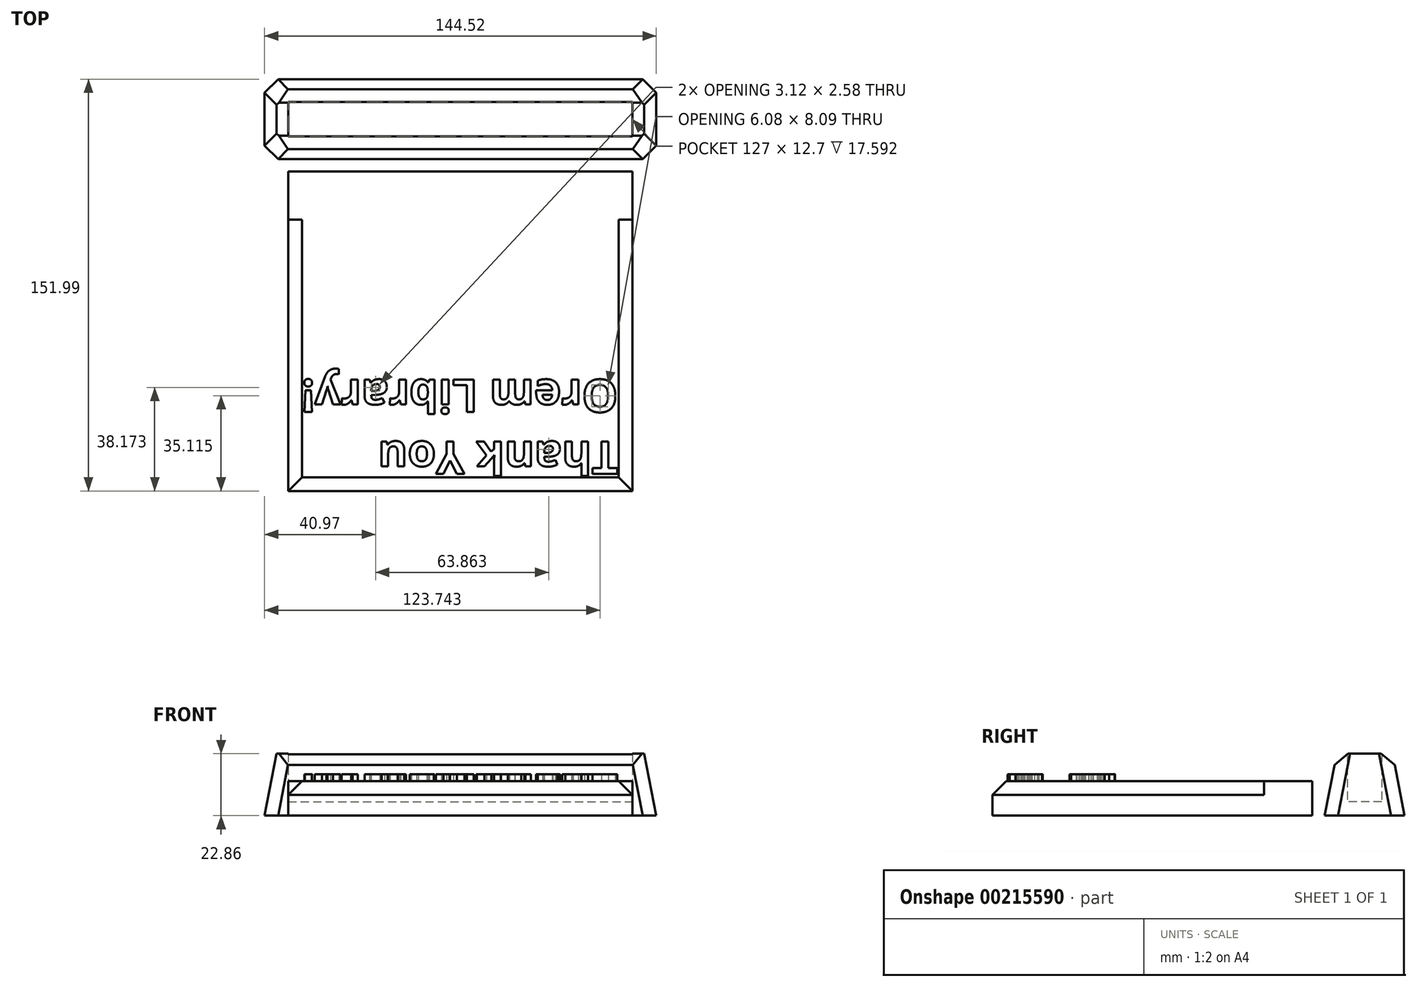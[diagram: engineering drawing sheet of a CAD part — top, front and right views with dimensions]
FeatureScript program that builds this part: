
annotation { "Feature Type Name" : "Feature", "Feature Type Description" : "" }
export const myFeature = defineFeature(function(context is Context, id is Id, definition is map)
    precondition{}
    {
        {
            var Q0;
            Q0=qCreatedBy(makeId("Top.planeOp"),FACE);
            var sketch = newSketch(context, id + "F0", { "sketchPlane" : qUnion([Q0])});
            skLineSegment(sketch, "E0.bottom", {"start": v(-63.5, 6.35) * mm, "end": v(63.5, 6.35) * mm});
            skLineSegment(sketch, "E0.top", {"start": v(-63.5, -6.35) * mm, "end": v(63.5, -6.35) * mm});
            skLineSegment(sketch, "E0.left", {"start": v(-63.5, 6.35) * mm, "end": v(-63.5, -6.35) * mm});
            skLineSegment(sketch, "E0.right", {"start": v(63.5, 6.35) * mm, "end": v(63.5, -6.35) * mm});
            skPoint(sketch, "E0.middle", {"position": v(0, 0) * mm});
            skSolve(sketch);
        }
        {
            var Q0;
            Q0=qCreatedBy(makeId("Top.planeOp"),FACE);
            var sketch = newSketch(context, id + "F1", { "sketchPlane" : qUnion([Q0])});
            skLineSegment(sketch, "E1.bottom", {"start": v(-67.81, 10.3) * mm, "end": v(67.81, 10.3) * mm});
            skLineSegment(sketch, "E1.top", {"start": v(-67.81, -10.3) * mm, "end": v(67.81, -10.3) * mm});
            skLineSegment(sketch, "E1.left", {"start": v(-67.81, 10.3) * mm, "end": v(-67.81, -10.3) * mm});
            skLineSegment(sketch, "E1.right", {"start": v(67.81, 10.3) * mm, "end": v(67.81, -10.3) * mm});
            skPoint(sketch, "E1.middle", {"position": v(0, 0) * mm});
            skSolve(sketch);
        }
        {
            var Q0;
            Q0=makeQuery(id+"F1.imprint","IMPRINT",FACE,{"disambiguationData":[TD([[makeQuery(id+"F1.imprint","IMPRINT",EDGE,{"derivedFrom":sQuery(id+"F1.wireOp",EDGE,"E1.bottom")}),-1.0]])]});
            extrude(context, id + "F2", {"entities" : qUnion([Q0]), "depth" : 22.86 * mm});
        }
        {
            var Q0;
            Q0=makeQuery(id+"F2.opExtrude","CAP_FACE",FACE,{"disambiguationData":[OSD([sQuery(id+"F1.wireOp",EDGE,"E1.bottom"),sQuery(id+"F1.wireOp",EDGE,"E1.top"),sQuery(id+"F1.wireOp",EDGE,"E1.left"),sQuery(id+"F1.wireOp",EDGE,"E1.right")])],"isStart":false});
            extrude(context, id + "F3", {"entities" : qUnion([Q0]), "operationType" : NewBodyOperationType.ADD, "oppositeDirection" : true, "depth" : 22.86 * mm, "hasDraft" : true, "draftAngle" : 11 * degree});
        }
        {
            var Q0;
            Q0=makeQuery(id+"F0.imprint","IMPRINT",FACE,{"disambiguationData":[TD([[makeQuery(id+"F0.imprint","IMPRINT",EDGE,{"derivedFrom":sQuery(id+"F0.wireOp",EDGE,"E0.bottom")}),-1.0]])]});
            extrude(context, id + "F4", {"entities" : qUnion([Q0]), "operationType" : NewBodyOperationType.REMOVE, "depth" : 25.4 * mm, "hasSecondDirection" : true, "secondDirectionOppositeDirection" : false, "secondDirectionDepth" : 5.08 * mm});
        }
        {
            var Q0;
            Q0=makeQuery(id+"F3.opExtrude","SWEPT_EDGE",EDGE,{"disambiguationData":[OSD([sQuery(id+"F1.wireOp",EDGE,"E1.top"),sQuery(id+"F1.wireOp",EDGE,"E1.left")])]});
            var Q1;
            Q1=makeQuery(id+"F3.opExtrude","SWEPT_EDGE",EDGE,{"disambiguationData":[OSD([sQuery(id+"F1.wireOp",EDGE,"E1.bottom"),sQuery(id+"F1.wireOp",EDGE,"E1.left")])]});
            var Q2;
            Q2=makeQuery(id+"F3.opExtrude","SWEPT_EDGE",EDGE,{"disambiguationData":[OSD([sQuery(id+"F1.wireOp",EDGE,"E1.top"),sQuery(id+"F1.wireOp",EDGE,"E1.right")])]});
            var Q3;
            Q3=makeQuery(id+"F3.opExtrude","SWEPT_EDGE",EDGE,{"disambiguationData":[OSD([sQuery(id+"F1.wireOp",EDGE,"E1.bottom"),sQuery(id+"F1.wireOp",EDGE,"E1.right")])]});
            var Q4;
            {var subQ0=sQuery(id+"F1.wireOp",EDGE,"E1.top");Q4=makeQuery(id+"F3.boolean.opBoolean","MERGE",EDGE,{"derivedFrom":[makeQuery(id+"F2.opExtrude","CAP_EDGE",EDGE,{"disambiguationData":[OSD([subQ0])],"isStart":false}),makeQuery(id+"F3.opExtrude","CAP_EDGE",EDGE,{"disambiguationData":[OSD([subQ0])],"isStart":true})]});}
            var Q5;
            {var subQ0=sQuery(id+"F1.wireOp",EDGE,"E1.bottom");Q5=makeQuery(id+"F3.boolean.opBoolean","MERGE",EDGE,{"derivedFrom":[makeQuery(id+"F2.opExtrude","CAP_EDGE",EDGE,{"disambiguationData":[OSD([subQ0])],"isStart":false}),makeQuery(id+"F3.opExtrude","CAP_EDGE",EDGE,{"disambiguationData":[OSD([subQ0])],"isStart":true})]});}
            chamfer(context, id + "F5", {"entities" : qUnion([Q0, Q1, Q2, Q3, Q4, Q5]), "width" : 5.08 * mm, "tangentPropagation" : true});
        }
        {
            var Q0;
            Q0=makeQuery(id+"F2.opExtrude","SWEPT_BODY",BODY,{"disambiguationData":[OSD([sQuery(id+"F1.wireOp",EDGE,"E1.bottom"),sQuery(id+"F1.wireOp",EDGE,"E1.top"),sQuery(id+"F1.wireOp",EDGE,"E1.left"),sQuery(id+"F1.wireOp",EDGE,"E1.right")])]});
            transform(context, id + "F6", {"entities" : qUnion([Q0]), "transformType" : TransformType.TRANSLATION_3D, "dx" : 0 * mm, "dy" : 56.13 * mm, "dz" : 0 * mm, "makeCopy" : false});
        }
        {
            var Q0;
            Q0=qCreatedBy(makeId("Top.planeOp"),FACE);
            var sketch = newSketch(context, id + "F7", { "sketchPlane" : qUnion([Q0])});
            skLineSegment(sketch, "E2.bottom", {"start": v(-63.5, 36.8) * mm, "end": v(63.5, 36.8) * mm});
            skLineSegment(sketch, "E2.top", {"start": v(-63.5, -81.1) * mm, "end": v(63.5, -81.1) * mm});
            skLineSegment(sketch, "E2.left", {"start": v(-63.5, 36.8) * mm, "end": v(-63.5, -81.1) * mm});
            skLineSegment(sketch, "E2.right", {"start": v(63.5, 36.8) * mm, "end": v(63.5, -81.1) * mm});
            skPoint(sketch, "E2.middle", {"position": v(0, -22.14) * mm});
            skSolve(sketch);
        }
        {
            var Q0;
            Q0=makeQuery(id+"F7.imprint","IMPRINT",FACE,{"disambiguationData":[TD([[makeQuery(id+"F7.imprint","IMPRINT",EDGE,{"derivedFrom":sQuery(id+"F7.wireOp",EDGE,"E2.bottom")}),-1.0]])]});
            extrude(context, id + "F8", {"entities" : qUnion([Q0]), "depth" : 12.7 * mm});
        }
        {
            var Q0;
            Q0=makeQuery(id+"F8.opExtrude","CAP_EDGE",EDGE,{"disambiguationData":[OSD([sQuery(id+"F7.wireOp",EDGE,"E2.top")])],"isStart":false});
            var Q1;
            Q1=makeQuery(id+"F8.opExtrude","CAP_EDGE",EDGE,{"disambiguationData":[OSD([sQuery(id+"F7.wireOp",EDGE,"E2.right")])],"isStart":false});
            var Q2;
            Q2=makeQuery(id+"F8.opExtrude","CAP_EDGE",EDGE,{"disambiguationData":[OSD([sQuery(id+"F7.wireOp",EDGE,"E2.left")])],"isStart":false});
            chamfer(context, id + "F9", {"entities" : qUnion([Q0, Q1, Q2]), "width" : 5.08 * mm, "tangentPropagation" : true});
        }
        {
            var Q0;
            Q0=makeQuery(id+"F8.opExtrude","SWEPT_FACE",FACE,{"disambiguationData":[OSD([sQuery(id+"F7.wireOp",EDGE,"E2.bottom")])]});
            var sketch = newSketch(context, id + "F10", { "sketchPlane" : qUnion([Q0])});
            skLineSegment(sketch, "E3.bottom", {"start": v(-63.5, 0) * mm, "end": v(-10.71, 0) * mm});
            skLineSegment(sketch, "E3.top", {"start": v(-63.5, 12.7) * mm, "end": v(-10.71, 12.7) * mm});
            skLineSegment(sketch, "E3.left", {"start": v(-63.5, 0) * mm, "end": v(-63.5, 12.7) * mm});
            skLineSegment(sketch, "E3.right", {"start": v(-10.71, 0) * mm, "end": v(-10.71, 12.7) * mm});
            skLineSegment(sketch, "E4.bottom", {"start": v(-10.71, 12.7) * mm, "end": v(63.5, 12.7) * mm});
            skLineSegment(sketch, "E4.top", {"start": v(-10.71, 0) * mm, "end": v(63.5, 0) * mm});
            skLineSegment(sketch, "E4.left", {"start": v(-10.71, 12.7) * mm, "end": v(-10.71, 0) * mm});
            skLineSegment(sketch, "E4.right", {"start": v(63.5, 12.7) * mm, "end": v(63.5, 0) * mm});
            skSolve(sketch);
        }
        {
            var Q0;
            {var subQ1=makeQuery(id+"F9.opChamfer","BLEND_EDGE",EDGE,{"blendedFrom":[makeQuery(id+"F8.opExtrude","CAP_EDGE",EDGE,{"disambiguationData":[OSD([sQuery(id+"F7.wireOp",EDGE,"E2.right")])],"isStart":false}),makeQuery(id+"F8.opExtrude","SWEPT_FACE",FACE,{"disambiguationData":[OSD([sQuery(id+"F7.wireOp",EDGE,"E2.bottom")])]})],"blendedInto":[makeQuery(id+"F8.opExtrude","SWEPT_FACE",FACE,{"disambiguationData":[OSD([sQuery(id+"F7.wireOp",EDGE,"E2.bottom")])]})]});Q0=makeQuery(id+"F10.imprint","IMPRINT",FACE,{"disambiguationData":[TD([[makeQuery(id+"F10.imprint","IMPRINT",EDGE,{"derivedFrom":subQ1}),-1.0]])]});}
            var Q1;
            {var subQ2=sQuery(id+"F10.wireOp",EDGE,"E3.bottom");Q1=makeQuery(id+"F10.imprint","IMPRINT",FACE,{"disambiguationData":[TD([[makeQuery(id+"F10.imprint","IMPRINT",EDGE,{"derivedFrom":subQ2}),-1.0]])]});}
            var Q2;
            {var subQ1=makeQuery(id+"F9.opChamfer","BLEND_EDGE",EDGE,{"blendedFrom":[makeQuery(id+"F8.opExtrude","CAP_EDGE",EDGE,{"disambiguationData":[OSD([sQuery(id+"F7.wireOp",EDGE,"E2.left")])],"isStart":false}),makeQuery(id+"F8.opExtrude","SWEPT_FACE",FACE,{"disambiguationData":[OSD([sQuery(id+"F7.wireOp",EDGE,"E2.bottom")])]})],"blendedInto":[makeQuery(id+"F8.opExtrude","SWEPT_FACE",FACE,{"disambiguationData":[OSD([sQuery(id+"F7.wireOp",EDGE,"E2.bottom")])]})]});Q2=makeQuery(id+"F10.imprint","IMPRINT",FACE,{"disambiguationData":[TD([[makeQuery(id+"F10.imprint","IMPRINT",EDGE,{"derivedFrom":subQ1}),-1.0]])]});}
            var Q3;
            {var subQ1=sQuery(id+"F10.wireOp",EDGE,"E4.top");Q3=makeQuery(id+"F10.imprint","IMPRINT",FACE,{"disambiguationData":[TD([[makeQuery(id+"F10.imprint","IMPRINT",EDGE,{"derivedFrom":subQ1}),-1.0]])]});}
            extrude(context, id + "F11", {"entities" : qUnion([Q0, Q1, Q2, Q3]), "operationType" : NewBodyOperationType.ADD, "oppositeDirection" : true, "depth" : 17.78 * mm});
        }
        {
            var Q0;
            Q0=makeQuery(id+"F11.boolean.opBoolean","MERGE",FACE,{"derivedFrom":[makeQuery(id+"F8.opExtrude","CAP_FACE",FACE,{"disambiguationData":[OSD([sQuery(id+"F7.wireOp",EDGE,"E2.bottom"),sQuery(id+"F7.wireOp",EDGE,"E2.top"),sQuery(id+"F7.wireOp",EDGE,"E2.left"),sQuery(id+"F7.wireOp",EDGE,"E2.right")])],"isStart":false}),makeQuery(id+"F11.opExtrude","SWEPT_FACE",FACE,{"disambiguationData":[OSD([sQuery(id+"F10.wireOp",EDGE,"E3.top"),sQuery(id+"F10.wireOp",EDGE,"E4.bottom")])]})]});
            var sketch = newSketch(context, id + "F12", { "sketchPlane" : qUnion([Q0])});
            skText(sketch, "E5", { "text": "Thank You\nOrem Library!", "fontName": "OpenSans-Bold.ttf"});
            const initialGuessF12  = {"E5": [-0.05842, -0.07602, 1, 0, 0.01209]};
            skSetInitialGuess(sketch, initialGuessF12);
            skSolve(sketch);
        }
        {
            var Q0;
            Q0 = qSketchRegion(id + "F12", true);
            extrude(context, id + "F13", {"entities" : qUnion([Q0]), "depth" : 2.54 * mm});
        }
        {
            var Q0;
            Q0=makeQuery(id+"F13.opExtrude","SWEPT_BODY",BODY,{"disambiguationData":[OSD([sQuery(id+"F12.wireOp",EDGE,"E5.sketch_text.stroke-0"),sQuery(id+"F12.wireOp",EDGE,"E5.sketch_text.stroke-1"),sQuery(id+"F12.wireOp",EDGE,"E5.sketch_text.stroke-2"),sQuery(id+"F12.wireOp",EDGE,"E5.sketch_text.stroke-3"),sQuery(id+"F12.wireOp",EDGE,"E5.sketch_text.stroke-4"),sQuery(id+"F12.wireOp",EDGE,"E5.sketch_text.stroke-5"),sQuery(id+"F12.wireOp",EDGE,"E5.sketch_text.stroke-6"),sQuery(id+"F12.wireOp",EDGE,"E5.sketch_text.stroke-7")])]});
            var Q1;
            Q1=makeQuery(id+"F13.opExtrude","SWEPT_BODY",BODY,{"disambiguationData":[OSD([sQuery(id+"F12.wireOp",EDGE,"E5.sketch_text.stroke-8"),sQuery(id+"F12.wireOp",EDGE,"E5.sketch_text.stroke-9"),sQuery(id+"F12.wireOp",EDGE,"E5.sketch_text.stroke-10"),sQuery(id+"F12.wireOp",EDGE,"E5.sketch_text.stroke-11"),sQuery(id+"F12.wireOp",EDGE,"E5.sketch_text.stroke-12"),sQuery(id+"F12.wireOp",EDGE,"E5.sketch_text.stroke-13"),sQuery(id+"F12.wireOp",EDGE,"E5.sketch_text.stroke-14"),sQuery(id+"F12.wireOp",EDGE,"E5.sketch_text.stroke-15"),sQuery(id+"F12.wireOp",EDGE,"E5.sketch_text.stroke-16"),sQuery(id+"F12.wireOp",EDGE,"E5.sketch_text.stroke-17"),sQuery(id+"F12.wireOp",EDGE,"E5.sketch_text.stroke-18"),sQuery(id+"F12.wireOp",EDGE,"E5.sketch_text.stroke-19"),sQuery(id+"F12.wireOp",EDGE,"E5.sketch_text.stroke-20"),sQuery(id+"F12.wireOp",EDGE,"E5.sketch_text.stroke-21"),sQuery(id+"F12.wireOp",EDGE,"E5.sketch_text.stroke-22"),sQuery(id+"F12.wireOp",EDGE,"E5.sketch_text.stroke-23"),sQuery(id+"F12.wireOp",EDGE,"E5.sketch_text.stroke-24")])]});
            var Q2;
            Q2=makeQuery(id+"F13.opExtrude","SWEPT_BODY",BODY,{"disambiguationData":[OSD([sQuery(id+"F12.wireOp",EDGE,"E5.sketch_text.stroke-25"),sQuery(id+"F12.wireOp",EDGE,"E5.sketch_text.stroke-26"),sQuery(id+"F12.wireOp",EDGE,"E5.sketch_text.stroke-27"),sQuery(id+"F12.wireOp",EDGE,"E5.sketch_text.stroke-28"),sQuery(id+"F12.wireOp",EDGE,"E5.sketch_text.stroke-29"),sQuery(id+"F12.wireOp",EDGE,"E5.sketch_text.stroke-30"),sQuery(id+"F12.wireOp",EDGE,"E5.sketch_text.stroke-31"),sQuery(id+"F12.wireOp",EDGE,"E5.sketch_text.stroke-32"),sQuery(id+"F12.wireOp",EDGE,"E5.sketch_text.stroke-33"),sQuery(id+"F12.wireOp",EDGE,"E5.sketch_text.stroke-34"),sQuery(id+"F12.wireOp",EDGE,"E5.sketch_text.stroke-35"),sQuery(id+"F12.wireOp",EDGE,"E5.sketch_text.stroke-36"),sQuery(id+"F12.wireOp",EDGE,"E5.sketch_text.stroke-37"),sQuery(id+"F12.wireOp",EDGE,"E5.sketch_text.stroke-38"),sQuery(id+"F12.wireOp",EDGE,"E5.sketch_text.stroke-39"),sQuery(id+"F12.wireOp",EDGE,"E5.sketch_text.stroke-40"),sQuery(id+"F12.wireOp",EDGE,"E5.sketch_text.stroke-41"),sQuery(id+"F12.wireOp",EDGE,"E5.sketch_text.stroke-42"),sQuery(id+"F12.wireOp",EDGE,"E5.sketch_text.stroke-43"),sQuery(id+"F12.wireOp",EDGE,"E5.sketch_text.stroke-44"),sQuery(id+"F12.wireOp",EDGE,"E5.sketch_text.stroke-45"),sQuery(id+"F12.wireOp",EDGE,"E5.sketch_text.stroke-46"),sQuery(id+"F12.wireOp",EDGE,"E5.sketch_text.stroke-47"),sQuery(id+"F12.wireOp",EDGE,"E5.sketch_text.stroke-48"),sQuery(id+"F12.wireOp",EDGE,"E5.sketch_text.stroke-49")])]});
            var Q3;
            Q3=makeQuery(id+"F13.opExtrude","SWEPT_BODY",BODY,{"disambiguationData":[OSD([sQuery(id+"F12.wireOp",EDGE,"E5.sketch_text.stroke-50"),sQuery(id+"F12.wireOp",EDGE,"E5.sketch_text.stroke-51"),sQuery(id+"F12.wireOp",EDGE,"E5.sketch_text.stroke-52"),sQuery(id+"F12.wireOp",EDGE,"E5.sketch_text.stroke-53"),sQuery(id+"F12.wireOp",EDGE,"E5.sketch_text.stroke-54"),sQuery(id+"F12.wireOp",EDGE,"E5.sketch_text.stroke-55"),sQuery(id+"F12.wireOp",EDGE,"E5.sketch_text.stroke-56"),sQuery(id+"F12.wireOp",EDGE,"E5.sketch_text.stroke-57"),sQuery(id+"F12.wireOp",EDGE,"E5.sketch_text.stroke-58"),sQuery(id+"F12.wireOp",EDGE,"E5.sketch_text.stroke-59"),sQuery(id+"F12.wireOp",EDGE,"E5.sketch_text.stroke-60"),sQuery(id+"F12.wireOp",EDGE,"E5.sketch_text.stroke-61"),sQuery(id+"F12.wireOp",EDGE,"E5.sketch_text.stroke-62"),sQuery(id+"F12.wireOp",EDGE,"E5.sketch_text.stroke-63"),sQuery(id+"F12.wireOp",EDGE,"E5.sketch_text.stroke-64"),sQuery(id+"F12.wireOp",EDGE,"E5.sketch_text.stroke-65"),sQuery(id+"F12.wireOp",EDGE,"E5.sketch_text.stroke-66")])]});
            var Q4;
            Q4=makeQuery(id+"F13.opExtrude","SWEPT_BODY",BODY,{"disambiguationData":[OSD([sQuery(id+"F12.wireOp",EDGE,"E5.sketch_text.stroke-67"),sQuery(id+"F12.wireOp",EDGE,"E5.sketch_text.stroke-68"),sQuery(id+"F12.wireOp",EDGE,"E5.sketch_text.stroke-69"),sQuery(id+"F12.wireOp",EDGE,"E5.sketch_text.stroke-70"),sQuery(id+"F12.wireOp",EDGE,"E5.sketch_text.stroke-71"),sQuery(id+"F12.wireOp",EDGE,"E5.sketch_text.stroke-72"),sQuery(id+"F12.wireOp",EDGE,"E5.sketch_text.stroke-73"),sQuery(id+"F12.wireOp",EDGE,"E5.sketch_text.stroke-74"),sQuery(id+"F12.wireOp",EDGE,"E5.sketch_text.stroke-75"),sQuery(id+"F12.wireOp",EDGE,"E5.sketch_text.stroke-76"),sQuery(id+"F12.wireOp",EDGE,"E5.sketch_text.stroke-77"),sQuery(id+"F12.wireOp",EDGE,"E5.sketch_text.stroke-78"),sQuery(id+"F12.wireOp",EDGE,"E5.sketch_text.stroke-79"),sQuery(id+"F12.wireOp",EDGE,"E5.sketch_text.stroke-80"),sQuery(id+"F12.wireOp",EDGE,"E5.sketch_text.stroke-81")])]});
            var Q5;
            Q5=makeQuery(id+"F13.opExtrude","SWEPT_BODY",BODY,{"disambiguationData":[OSD([sQuery(id+"F12.wireOp",EDGE,"E5.sketch_text.stroke-82"),sQuery(id+"F12.wireOp",EDGE,"E5.sketch_text.stroke-83"),sQuery(id+"F12.wireOp",EDGE,"E5.sketch_text.stroke-84"),sQuery(id+"F12.wireOp",EDGE,"E5.sketch_text.stroke-85"),sQuery(id+"F12.wireOp",EDGE,"E5.sketch_text.stroke-86"),sQuery(id+"F12.wireOp",EDGE,"E5.sketch_text.stroke-87"),sQuery(id+"F12.wireOp",EDGE,"E5.sketch_text.stroke-88"),sQuery(id+"F12.wireOp",EDGE,"E5.sketch_text.stroke-89"),sQuery(id+"F12.wireOp",EDGE,"E5.sketch_text.stroke-90")])]});
            var Q6;
            Q6=makeQuery(id+"F13.opExtrude","SWEPT_BODY",BODY,{"disambiguationData":[OSD([sQuery(id+"F12.wireOp",EDGE,"E5.sketch_text.stroke-91"),sQuery(id+"F12.wireOp",EDGE,"E5.sketch_text.stroke-92"),sQuery(id+"F12.wireOp",EDGE,"E5.sketch_text.stroke-93"),sQuery(id+"F12.wireOp",EDGE,"E5.sketch_text.stroke-94"),sQuery(id+"F12.wireOp",EDGE,"E5.sketch_text.stroke-95"),sQuery(id+"F12.wireOp",EDGE,"E5.sketch_text.stroke-96"),sQuery(id+"F12.wireOp",EDGE,"E5.sketch_text.stroke-97"),sQuery(id+"F12.wireOp",EDGE,"E5.sketch_text.stroke-98"),sQuery(id+"F12.wireOp",EDGE,"E5.sketch_text.stroke-99"),sQuery(id+"F12.wireOp",EDGE,"E5.sketch_text.stroke-100"),sQuery(id+"F12.wireOp",EDGE,"E5.sketch_text.stroke-101"),sQuery(id+"F12.wireOp",EDGE,"E5.sketch_text.stroke-102"),sQuery(id+"F12.wireOp",EDGE,"E5.sketch_text.stroke-103"),sQuery(id+"F12.wireOp",EDGE,"E5.sketch_text.stroke-104"),sQuery(id+"F12.wireOp",EDGE,"E5.sketch_text.stroke-105"),sQuery(id+"F12.wireOp",EDGE,"E5.sketch_text.stroke-106"),sQuery(id+"F12.wireOp",EDGE,"E5.sketch_text.stroke-107"),sQuery(id+"F12.wireOp",EDGE,"E5.sketch_text.stroke-108")])]});
            var Q7;
            Q7=makeQuery(id+"F13.opExtrude","SWEPT_BODY",BODY,{"disambiguationData":[OSD([sQuery(id+"F12.wireOp",EDGE,"E5.sketch_text.stroke-109"),sQuery(id+"F12.wireOp",EDGE,"E5.sketch_text.stroke-110"),sQuery(id+"F12.wireOp",EDGE,"E5.sketch_text.stroke-111"),sQuery(id+"F12.wireOp",EDGE,"E5.sketch_text.stroke-112"),sQuery(id+"F12.wireOp",EDGE,"E5.sketch_text.stroke-113"),sQuery(id+"F12.wireOp",EDGE,"E5.sketch_text.stroke-114"),sQuery(id+"F12.wireOp",EDGE,"E5.sketch_text.stroke-115"),sQuery(id+"F12.wireOp",EDGE,"E5.sketch_text.stroke-116"),sQuery(id+"F12.wireOp",EDGE,"E5.sketch_text.stroke-117"),sQuery(id+"F12.wireOp",EDGE,"E5.sketch_text.stroke-118"),sQuery(id+"F12.wireOp",EDGE,"E5.sketch_text.stroke-119"),sQuery(id+"F12.wireOp",EDGE,"E5.sketch_text.stroke-120"),sQuery(id+"F12.wireOp",EDGE,"E5.sketch_text.stroke-121"),sQuery(id+"F12.wireOp",EDGE,"E5.sketch_text.stroke-122"),sQuery(id+"F12.wireOp",EDGE,"E5.sketch_text.stroke-123"),sQuery(id+"F12.wireOp",EDGE,"E5.sketch_text.stroke-124"),sQuery(id+"F12.wireOp",EDGE,"E5.sketch_text.stroke-125")])]});
            var Q8;
            Q8=makeQuery(id+"F13.opExtrude","SWEPT_BODY",BODY,{"disambiguationData":[OSD([sQuery(id+"F12.wireOp",EDGE,"E5.sketch_text.stroke-126"),sQuery(id+"F12.wireOp",EDGE,"E5.sketch_text.stroke-127"),sQuery(id+"F12.wireOp",EDGE,"E5.sketch_text.stroke-128"),sQuery(id+"F12.wireOp",EDGE,"E5.sketch_text.stroke-129"),sQuery(id+"F12.wireOp",EDGE,"E5.sketch_text.stroke-130"),sQuery(id+"F12.wireOp",EDGE,"E5.sketch_text.stroke-131"),sQuery(id+"F12.wireOp",EDGE,"E5.sketch_text.stroke-132"),sQuery(id+"F12.wireOp",EDGE,"E5.sketch_text.stroke-133"),sQuery(id+"F12.wireOp",EDGE,"E5.sketch_text.stroke-134"),sQuery(id+"F12.wireOp",EDGE,"E5.sketch_text.stroke-135"),sQuery(id+"F12.wireOp",EDGE,"E5.sketch_text.stroke-136"),sQuery(id+"F12.wireOp",EDGE,"E5.sketch_text.stroke-137"),sQuery(id+"F12.wireOp",EDGE,"E5.sketch_text.stroke-138"),sQuery(id+"F12.wireOp",EDGE,"E5.sketch_text.stroke-139")])]});
            var Q9;
            Q9=makeQuery(id+"F13.opExtrude","SWEPT_BODY",BODY,{"disambiguationData":[OSD([sQuery(id+"F12.wireOp",EDGE,"E5.sketch_text.stroke-140"),sQuery(id+"F12.wireOp",EDGE,"E5.sketch_text.stroke-141"),sQuery(id+"F12.wireOp",EDGE,"E5.sketch_text.stroke-142"),sQuery(id+"F12.wireOp",EDGE,"E5.sketch_text.stroke-143"),sQuery(id+"F12.wireOp",EDGE,"E5.sketch_text.stroke-144"),sQuery(id+"F12.wireOp",EDGE,"E5.sketch_text.stroke-145"),sQuery(id+"F12.wireOp",EDGE,"E5.sketch_text.stroke-146"),sQuery(id+"F12.wireOp",EDGE,"E5.sketch_text.stroke-147"),sQuery(id+"F12.wireOp",EDGE,"E5.sketch_text.stroke-148"),sQuery(id+"F12.wireOp",EDGE,"E5.sketch_text.stroke-149"),sQuery(id+"F12.wireOp",EDGE,"E5.sketch_text.stroke-150"),sQuery(id+"F12.wireOp",EDGE,"E5.sketch_text.stroke-151"),sQuery(id+"F12.wireOp",EDGE,"E5.sketch_text.stroke-152")])]});
            var Q10;
            Q10=makeQuery(id+"F13.opExtrude","SWEPT_BODY",BODY,{"disambiguationData":[OSD([sQuery(id+"F12.wireOp",EDGE,"E5.sketch_text.stroke-153"),sQuery(id+"F12.wireOp",EDGE,"E5.sketch_text.stroke-154"),sQuery(id+"F12.wireOp",EDGE,"E5.sketch_text.stroke-155"),sQuery(id+"F12.wireOp",EDGE,"E5.sketch_text.stroke-156"),sQuery(id+"F12.wireOp",EDGE,"E5.sketch_text.stroke-157"),sQuery(id+"F12.wireOp",EDGE,"E5.sketch_text.stroke-158"),sQuery(id+"F12.wireOp",EDGE,"E5.sketch_text.stroke-159"),sQuery(id+"F12.wireOp",EDGE,"E5.sketch_text.stroke-160"),sQuery(id+"F12.wireOp",EDGE,"E5.sketch_text.stroke-161"),sQuery(id+"F12.wireOp",EDGE,"E5.sketch_text.stroke-162"),sQuery(id+"F12.wireOp",EDGE,"E5.sketch_text.stroke-163"),sQuery(id+"F12.wireOp",EDGE,"E5.sketch_text.stroke-164"),sQuery(id+"F12.wireOp",EDGE,"E5.sketch_text.stroke-165"),sQuery(id+"F12.wireOp",EDGE,"E5.sketch_text.stroke-166"),sQuery(id+"F12.wireOp",EDGE,"E5.sketch_text.stroke-167"),sQuery(id+"F12.wireOp",EDGE,"E5.sketch_text.stroke-168"),sQuery(id+"F12.wireOp",EDGE,"E5.sketch_text.stroke-169"),sQuery(id+"F12.wireOp",EDGE,"E5.sketch_text.stroke-170"),sQuery(id+"F12.wireOp",EDGE,"E5.sketch_text.stroke-171"),sQuery(id+"F12.wireOp",EDGE,"E5.sketch_text.stroke-172")])]});
            var Q11;
            Q11=makeQuery(id+"F13.opExtrude","SWEPT_BODY",BODY,{"disambiguationData":[OSD([sQuery(id+"F12.wireOp",EDGE,"E5.sketch_text.stroke-173"),sQuery(id+"F12.wireOp",EDGE,"E5.sketch_text.stroke-174"),sQuery(id+"F12.wireOp",EDGE,"E5.sketch_text.stroke-175"),sQuery(id+"F12.wireOp",EDGE,"E5.sketch_text.stroke-176"),sQuery(id+"F12.wireOp",EDGE,"E5.sketch_text.stroke-177"),sQuery(id+"F12.wireOp",EDGE,"E5.sketch_text.stroke-178"),sQuery(id+"F12.wireOp",EDGE,"E5.sketch_text.stroke-179"),sQuery(id+"F12.wireOp",EDGE,"E5.sketch_text.stroke-180"),sQuery(id+"F12.wireOp",EDGE,"E5.sketch_text.stroke-181"),sQuery(id+"F12.wireOp",EDGE,"E5.sketch_text.stroke-182"),sQuery(id+"F12.wireOp",EDGE,"E5.sketch_text.stroke-183"),sQuery(id+"F12.wireOp",EDGE,"E5.sketch_text.stroke-184"),sQuery(id+"F12.wireOp",EDGE,"E5.sketch_text.stroke-185"),sQuery(id+"F12.wireOp",EDGE,"E5.sketch_text.stroke-186"),sQuery(id+"F12.wireOp",EDGE,"E5.sketch_text.stroke-187"),sQuery(id+"F12.wireOp",EDGE,"E5.sketch_text.stroke-188"),sQuery(id+"F12.wireOp",EDGE,"E5.sketch_text.stroke-189"),sQuery(id+"F12.wireOp",EDGE,"E5.sketch_text.stroke-190"),sQuery(id+"F12.wireOp",EDGE,"E5.sketch_text.stroke-191"),sQuery(id+"F12.wireOp",EDGE,"E5.sketch_text.stroke-192"),sQuery(id+"F12.wireOp",EDGE,"E5.sketch_text.stroke-193"),sQuery(id+"F12.wireOp",EDGE,"E5.sketch_text.stroke-194"),sQuery(id+"F12.wireOp",EDGE,"E5.sketch_text.stroke-195"),sQuery(id+"F12.wireOp",EDGE,"E5.sketch_text.stroke-196"),sQuery(id+"F12.wireOp",EDGE,"E5.sketch_text.stroke-197"),sQuery(id+"F12.wireOp",EDGE,"E5.sketch_text.stroke-198"),sQuery(id+"F12.wireOp",EDGE,"E5.sketch_text.stroke-199"),sQuery(id+"F12.wireOp",EDGE,"E5.sketch_text.stroke-200")])]});
            var Q12;
            Q12=makeQuery(id+"F13.opExtrude","SWEPT_BODY",BODY,{"disambiguationData":[OSD([sQuery(id+"F12.wireOp",EDGE,"E5.sketch_text.stroke-201"),sQuery(id+"F12.wireOp",EDGE,"E5.sketch_text.stroke-202"),sQuery(id+"F12.wireOp",EDGE,"E5.sketch_text.stroke-203"),sQuery(id+"F12.wireOp",EDGE,"E5.sketch_text.stroke-204"),sQuery(id+"F12.wireOp",EDGE,"E5.sketch_text.stroke-205"),sQuery(id+"F12.wireOp",EDGE,"E5.sketch_text.stroke-206")])]});
            var Q13;
            Q13=makeQuery(id+"F13.opExtrude","SWEPT_BODY",BODY,{"disambiguationData":[OSD([sQuery(id+"F12.wireOp",EDGE,"E5.sketch_text.stroke-207"),sQuery(id+"F12.wireOp",EDGE,"E5.sketch_text.stroke-208"),sQuery(id+"F12.wireOp",EDGE,"E5.sketch_text.stroke-209"),sQuery(id+"F12.wireOp",EDGE,"E5.sketch_text.stroke-210"),sQuery(id+"F12.wireOp",EDGE,"E5.sketch_text.stroke-211")])]});
            var Q14;
            Q14=makeQuery(id+"F13.opExtrude","SWEPT_BODY",BODY,{"disambiguationData":[OSD([sQuery(id+"F12.wireOp",EDGE,"E5.sketch_text.stroke-212"),sQuery(id+"F12.wireOp",EDGE,"E5.sketch_text.stroke-213"),sQuery(id+"F12.wireOp",EDGE,"E5.sketch_text.stroke-214"),sQuery(id+"F12.wireOp",EDGE,"E5.sketch_text.stroke-215")])]});
            var Q15;
            Q15=makeQuery(id+"F13.opExtrude","SWEPT_BODY",BODY,{"disambiguationData":[OSD([sQuery(id+"F12.wireOp",EDGE,"E5.sketch_text.stroke-216"),sQuery(id+"F12.wireOp",EDGE,"E5.sketch_text.stroke-217"),sQuery(id+"F12.wireOp",EDGE,"E5.sketch_text.stroke-218"),sQuery(id+"F12.wireOp",EDGE,"E5.sketch_text.stroke-219"),sQuery(id+"F12.wireOp",EDGE,"E5.sketch_text.stroke-220"),sQuery(id+"F12.wireOp",EDGE,"E5.sketch_text.stroke-221"),sQuery(id+"F12.wireOp",EDGE,"E5.sketch_text.stroke-222"),sQuery(id+"F12.wireOp",EDGE,"E5.sketch_text.stroke-223"),sQuery(id+"F12.wireOp",EDGE,"E5.sketch_text.stroke-224"),sQuery(id+"F12.wireOp",EDGE,"E5.sketch_text.stroke-225"),sQuery(id+"F12.wireOp",EDGE,"E5.sketch_text.stroke-226"),sQuery(id+"F12.wireOp",EDGE,"E5.sketch_text.stroke-227"),sQuery(id+"F12.wireOp",EDGE,"E5.sketch_text.stroke-228"),sQuery(id+"F12.wireOp",EDGE,"E5.sketch_text.stroke-229"),sQuery(id+"F12.wireOp",EDGE,"E5.sketch_text.stroke-230"),sQuery(id+"F12.wireOp",EDGE,"E5.sketch_text.stroke-231"),sQuery(id+"F12.wireOp",EDGE,"E5.sketch_text.stroke-232"),sQuery(id+"F12.wireOp",EDGE,"E5.sketch_text.stroke-233"),sQuery(id+"F12.wireOp",EDGE,"E5.sketch_text.stroke-234"),sQuery(id+"F12.wireOp",EDGE,"E5.sketch_text.stroke-235"),sQuery(id+"F12.wireOp",EDGE,"E5.sketch_text.stroke-236"),sQuery(id+"F12.wireOp",EDGE,"E5.sketch_text.stroke-237"),sQuery(id+"F12.wireOp",EDGE,"E5.sketch_text.stroke-238")])]});
            var Q16;
            Q16=makeQuery(id+"F13.opExtrude","SWEPT_BODY",BODY,{"disambiguationData":[OSD([sQuery(id+"F12.wireOp",EDGE,"E5.sketch_text.stroke-239"),sQuery(id+"F12.wireOp",EDGE,"E5.sketch_text.stroke-240"),sQuery(id+"F12.wireOp",EDGE,"E5.sketch_text.stroke-241"),sQuery(id+"F12.wireOp",EDGE,"E5.sketch_text.stroke-242"),sQuery(id+"F12.wireOp",EDGE,"E5.sketch_text.stroke-243"),sQuery(id+"F12.wireOp",EDGE,"E5.sketch_text.stroke-244"),sQuery(id+"F12.wireOp",EDGE,"E5.sketch_text.stroke-245"),sQuery(id+"F12.wireOp",EDGE,"E5.sketch_text.stroke-246"),sQuery(id+"F12.wireOp",EDGE,"E5.sketch_text.stroke-247"),sQuery(id+"F12.wireOp",EDGE,"E5.sketch_text.stroke-248"),sQuery(id+"F12.wireOp",EDGE,"E5.sketch_text.stroke-249"),sQuery(id+"F12.wireOp",EDGE,"E5.sketch_text.stroke-250"),sQuery(id+"F12.wireOp",EDGE,"E5.sketch_text.stroke-251")])]});
            var Q17;
            Q17=makeQuery(id+"F13.opExtrude","SWEPT_BODY",BODY,{"disambiguationData":[OSD([sQuery(id+"F12.wireOp",EDGE,"E5.sketch_text.stroke-252"),sQuery(id+"F12.wireOp",EDGE,"E5.sketch_text.stroke-253"),sQuery(id+"F12.wireOp",EDGE,"E5.sketch_text.stroke-254"),sQuery(id+"F12.wireOp",EDGE,"E5.sketch_text.stroke-255"),sQuery(id+"F12.wireOp",EDGE,"E5.sketch_text.stroke-256"),sQuery(id+"F12.wireOp",EDGE,"E5.sketch_text.stroke-257"),sQuery(id+"F12.wireOp",EDGE,"E5.sketch_text.stroke-258"),sQuery(id+"F12.wireOp",EDGE,"E5.sketch_text.stroke-259"),sQuery(id+"F12.wireOp",EDGE,"E5.sketch_text.stroke-260"),sQuery(id+"F12.wireOp",EDGE,"E5.sketch_text.stroke-261"),sQuery(id+"F12.wireOp",EDGE,"E5.sketch_text.stroke-262"),sQuery(id+"F12.wireOp",EDGE,"E5.sketch_text.stroke-263"),sQuery(id+"F12.wireOp",EDGE,"E5.sketch_text.stroke-264"),sQuery(id+"F12.wireOp",EDGE,"E5.sketch_text.stroke-265"),sQuery(id+"F12.wireOp",EDGE,"E5.sketch_text.stroke-266"),sQuery(id+"F12.wireOp",EDGE,"E5.sketch_text.stroke-267"),sQuery(id+"F12.wireOp",EDGE,"E5.sketch_text.stroke-268"),sQuery(id+"F12.wireOp",EDGE,"E5.sketch_text.stroke-269"),sQuery(id+"F12.wireOp",EDGE,"E5.sketch_text.stroke-270"),sQuery(id+"F12.wireOp",EDGE,"E5.sketch_text.stroke-271"),sQuery(id+"F12.wireOp",EDGE,"E5.sketch_text.stroke-272"),sQuery(id+"F12.wireOp",EDGE,"E5.sketch_text.stroke-273"),sQuery(id+"F12.wireOp",EDGE,"E5.sketch_text.stroke-274"),sQuery(id+"F12.wireOp",EDGE,"E5.sketch_text.stroke-275"),sQuery(id+"F12.wireOp",EDGE,"E5.sketch_text.stroke-276")])]});
            var Q18;
            Q18=makeQuery(id+"F13.opExtrude","SWEPT_BODY",BODY,{"disambiguationData":[OSD([sQuery(id+"F12.wireOp",EDGE,"E5.sketch_text.stroke-277"),sQuery(id+"F12.wireOp",EDGE,"E5.sketch_text.stroke-278"),sQuery(id+"F12.wireOp",EDGE,"E5.sketch_text.stroke-279"),sQuery(id+"F12.wireOp",EDGE,"E5.sketch_text.stroke-280"),sQuery(id+"F12.wireOp",EDGE,"E5.sketch_text.stroke-281"),sQuery(id+"F12.wireOp",EDGE,"E5.sketch_text.stroke-282"),sQuery(id+"F12.wireOp",EDGE,"E5.sketch_text.stroke-283"),sQuery(id+"F12.wireOp",EDGE,"E5.sketch_text.stroke-284"),sQuery(id+"F12.wireOp",EDGE,"E5.sketch_text.stroke-285"),sQuery(id+"F12.wireOp",EDGE,"E5.sketch_text.stroke-286"),sQuery(id+"F12.wireOp",EDGE,"E5.sketch_text.stroke-287"),sQuery(id+"F12.wireOp",EDGE,"E5.sketch_text.stroke-288"),sQuery(id+"F12.wireOp",EDGE,"E5.sketch_text.stroke-289")])]});
            var Q19;
            Q19=makeQuery(id+"F13.opExtrude","SWEPT_BODY",BODY,{"disambiguationData":[OSD([sQuery(id+"F12.wireOp",EDGE,"E5.sketch_text.stroke-290"),sQuery(id+"F12.wireOp",EDGE,"E5.sketch_text.stroke-291"),sQuery(id+"F12.wireOp",EDGE,"E5.sketch_text.stroke-292"),sQuery(id+"F12.wireOp",EDGE,"E5.sketch_text.stroke-293"),sQuery(id+"F12.wireOp",EDGE,"E5.sketch_text.stroke-294"),sQuery(id+"F12.wireOp",EDGE,"E5.sketch_text.stroke-295"),sQuery(id+"F12.wireOp",EDGE,"E5.sketch_text.stroke-296"),sQuery(id+"F12.wireOp",EDGE,"E5.sketch_text.stroke-297"),sQuery(id+"F12.wireOp",EDGE,"E5.sketch_text.stroke-298"),sQuery(id+"F12.wireOp",EDGE,"E5.sketch_text.stroke-299"),sQuery(id+"F12.wireOp",EDGE,"E5.sketch_text.stroke-300"),sQuery(id+"F12.wireOp",EDGE,"E5.sketch_text.stroke-301"),sQuery(id+"F12.wireOp",EDGE,"E5.sketch_text.stroke-302"),sQuery(id+"F12.wireOp",EDGE,"E5.sketch_text.stroke-303"),sQuery(id+"F12.wireOp",EDGE,"E5.sketch_text.stroke-304"),sQuery(id+"F12.wireOp",EDGE,"E5.sketch_text.stroke-305"),sQuery(id+"F12.wireOp",EDGE,"E5.sketch_text.stroke-306")])]});
            var Q20;
            Q20=makeQuery(id+"F13.opExtrude","SWEPT_BODY",BODY,{"disambiguationData":[OSD([sQuery(id+"F12.wireOp",EDGE,"E5.sketch_text.stroke-307"),sQuery(id+"F12.wireOp",EDGE,"E5.sketch_text.stroke-308"),sQuery(id+"F12.wireOp",EDGE,"E5.sketch_text.stroke-309"),sQuery(id+"F12.wireOp",EDGE,"E5.sketch_text.stroke-310")])]});
            var Q21;
            Q21=makeQuery(id+"F13.opExtrude","SWEPT_BODY",BODY,{"disambiguationData":[OSD([sQuery(id+"F12.wireOp",EDGE,"E5.sketch_text.stroke-311"),sQuery(id+"F12.wireOp",EDGE,"E5.sketch_text.stroke-312"),sQuery(id+"F12.wireOp",EDGE,"E5.sketch_text.stroke-313"),sQuery(id+"F12.wireOp",EDGE,"E5.sketch_text.stroke-314"),sQuery(id+"F12.wireOp",EDGE,"E5.sketch_text.stroke-315"),sQuery(id+"F12.wireOp",EDGE,"E5.sketch_text.stroke-316"),sQuery(id+"F12.wireOp",EDGE,"E5.sketch_text.stroke-317"),sQuery(id+"F12.wireOp",EDGE,"E5.sketch_text.stroke-318")])]});
            var Q22;
            Q22=makeQuery(id+"F8.opExtrude","SWEPT_EDGE",EDGE,{"disambiguationData":[OSD([sQuery(id+"F7.wireOp",EDGE,"E2.top"),sQuery(id+"F7.wireOp",EDGE,"E2.right")])]});
            transform(context, id + "F14", {"entities" : qUnion([Q0, Q1, Q2, Q3, Q4, Q5, Q6, Q7, Q8, Q9, Q10, Q11, Q12, Q13, Q14, Q15, Q16, Q17, Q18, Q19, Q20, Q21]), "transformType" : TransformType.ROTATION, "transformAxis" : qUnion([Q22]), "angle" : 180 * degree, "makeCopy" : false});
        }
        {
            var Q0;
            Q0=makeQuery(id+"F13.opExtrude","SWEPT_BODY",BODY,{"disambiguationData":[OSD([sQuery(id+"F12.wireOp",EDGE,"E5.sketch_text.stroke-0"),sQuery(id+"F12.wireOp",EDGE,"E5.sketch_text.stroke-1"),sQuery(id+"F12.wireOp",EDGE,"E5.sketch_text.stroke-2"),sQuery(id+"F12.wireOp",EDGE,"E5.sketch_text.stroke-3"),sQuery(id+"F12.wireOp",EDGE,"E5.sketch_text.stroke-4"),sQuery(id+"F12.wireOp",EDGE,"E5.sketch_text.stroke-5"),sQuery(id+"F12.wireOp",EDGE,"E5.sketch_text.stroke-6"),sQuery(id+"F12.wireOp",EDGE,"E5.sketch_text.stroke-7")])]});
            var Q1;
            Q1=makeQuery(id+"F13.opExtrude","SWEPT_BODY",BODY,{"disambiguationData":[OSD([sQuery(id+"F12.wireOp",EDGE,"E5.sketch_text.stroke-8"),sQuery(id+"F12.wireOp",EDGE,"E5.sketch_text.stroke-9"),sQuery(id+"F12.wireOp",EDGE,"E5.sketch_text.stroke-10"),sQuery(id+"F12.wireOp",EDGE,"E5.sketch_text.stroke-11"),sQuery(id+"F12.wireOp",EDGE,"E5.sketch_text.stroke-12"),sQuery(id+"F12.wireOp",EDGE,"E5.sketch_text.stroke-13"),sQuery(id+"F12.wireOp",EDGE,"E5.sketch_text.stroke-14"),sQuery(id+"F12.wireOp",EDGE,"E5.sketch_text.stroke-15"),sQuery(id+"F12.wireOp",EDGE,"E5.sketch_text.stroke-16"),sQuery(id+"F12.wireOp",EDGE,"E5.sketch_text.stroke-17"),sQuery(id+"F12.wireOp",EDGE,"E5.sketch_text.stroke-18"),sQuery(id+"F12.wireOp",EDGE,"E5.sketch_text.stroke-19"),sQuery(id+"F12.wireOp",EDGE,"E5.sketch_text.stroke-20"),sQuery(id+"F12.wireOp",EDGE,"E5.sketch_text.stroke-21"),sQuery(id+"F12.wireOp",EDGE,"E5.sketch_text.stroke-22"),sQuery(id+"F12.wireOp",EDGE,"E5.sketch_text.stroke-23"),sQuery(id+"F12.wireOp",EDGE,"E5.sketch_text.stroke-24")])]});
            var Q2;
            Q2=makeQuery(id+"F13.opExtrude","SWEPT_BODY",BODY,{"disambiguationData":[OSD([sQuery(id+"F12.wireOp",EDGE,"E5.sketch_text.stroke-25"),sQuery(id+"F12.wireOp",EDGE,"E5.sketch_text.stroke-26"),sQuery(id+"F12.wireOp",EDGE,"E5.sketch_text.stroke-27"),sQuery(id+"F12.wireOp",EDGE,"E5.sketch_text.stroke-28"),sQuery(id+"F12.wireOp",EDGE,"E5.sketch_text.stroke-29"),sQuery(id+"F12.wireOp",EDGE,"E5.sketch_text.stroke-30"),sQuery(id+"F12.wireOp",EDGE,"E5.sketch_text.stroke-31"),sQuery(id+"F12.wireOp",EDGE,"E5.sketch_text.stroke-32"),sQuery(id+"F12.wireOp",EDGE,"E5.sketch_text.stroke-33"),sQuery(id+"F12.wireOp",EDGE,"E5.sketch_text.stroke-34"),sQuery(id+"F12.wireOp",EDGE,"E5.sketch_text.stroke-35"),sQuery(id+"F12.wireOp",EDGE,"E5.sketch_text.stroke-36"),sQuery(id+"F12.wireOp",EDGE,"E5.sketch_text.stroke-37"),sQuery(id+"F12.wireOp",EDGE,"E5.sketch_text.stroke-38"),sQuery(id+"F12.wireOp",EDGE,"E5.sketch_text.stroke-39"),sQuery(id+"F12.wireOp",EDGE,"E5.sketch_text.stroke-40"),sQuery(id+"F12.wireOp",EDGE,"E5.sketch_text.stroke-41"),sQuery(id+"F12.wireOp",EDGE,"E5.sketch_text.stroke-42"),sQuery(id+"F12.wireOp",EDGE,"E5.sketch_text.stroke-43"),sQuery(id+"F12.wireOp",EDGE,"E5.sketch_text.stroke-44"),sQuery(id+"F12.wireOp",EDGE,"E5.sketch_text.stroke-45"),sQuery(id+"F12.wireOp",EDGE,"E5.sketch_text.stroke-46"),sQuery(id+"F12.wireOp",EDGE,"E5.sketch_text.stroke-47"),sQuery(id+"F12.wireOp",EDGE,"E5.sketch_text.stroke-48"),sQuery(id+"F12.wireOp",EDGE,"E5.sketch_text.stroke-49")])]});
            var Q3;
            Q3=makeQuery(id+"F13.opExtrude","SWEPT_BODY",BODY,{"disambiguationData":[OSD([sQuery(id+"F12.wireOp",EDGE,"E5.sketch_text.stroke-50"),sQuery(id+"F12.wireOp",EDGE,"E5.sketch_text.stroke-51"),sQuery(id+"F12.wireOp",EDGE,"E5.sketch_text.stroke-52"),sQuery(id+"F12.wireOp",EDGE,"E5.sketch_text.stroke-53"),sQuery(id+"F12.wireOp",EDGE,"E5.sketch_text.stroke-54"),sQuery(id+"F12.wireOp",EDGE,"E5.sketch_text.stroke-55"),sQuery(id+"F12.wireOp",EDGE,"E5.sketch_text.stroke-56"),sQuery(id+"F12.wireOp",EDGE,"E5.sketch_text.stroke-57"),sQuery(id+"F12.wireOp",EDGE,"E5.sketch_text.stroke-58"),sQuery(id+"F12.wireOp",EDGE,"E5.sketch_text.stroke-59"),sQuery(id+"F12.wireOp",EDGE,"E5.sketch_text.stroke-60"),sQuery(id+"F12.wireOp",EDGE,"E5.sketch_text.stroke-61"),sQuery(id+"F12.wireOp",EDGE,"E5.sketch_text.stroke-62"),sQuery(id+"F12.wireOp",EDGE,"E5.sketch_text.stroke-63"),sQuery(id+"F12.wireOp",EDGE,"E5.sketch_text.stroke-64"),sQuery(id+"F12.wireOp",EDGE,"E5.sketch_text.stroke-65"),sQuery(id+"F12.wireOp",EDGE,"E5.sketch_text.stroke-66")])]});
            var Q4;
            Q4=makeQuery(id+"F13.opExtrude","SWEPT_BODY",BODY,{"disambiguationData":[OSD([sQuery(id+"F12.wireOp",EDGE,"E5.sketch_text.stroke-67"),sQuery(id+"F12.wireOp",EDGE,"E5.sketch_text.stroke-68"),sQuery(id+"F12.wireOp",EDGE,"E5.sketch_text.stroke-69"),sQuery(id+"F12.wireOp",EDGE,"E5.sketch_text.stroke-70"),sQuery(id+"F12.wireOp",EDGE,"E5.sketch_text.stroke-71"),sQuery(id+"F12.wireOp",EDGE,"E5.sketch_text.stroke-72"),sQuery(id+"F12.wireOp",EDGE,"E5.sketch_text.stroke-73"),sQuery(id+"F12.wireOp",EDGE,"E5.sketch_text.stroke-74"),sQuery(id+"F12.wireOp",EDGE,"E5.sketch_text.stroke-75"),sQuery(id+"F12.wireOp",EDGE,"E5.sketch_text.stroke-76"),sQuery(id+"F12.wireOp",EDGE,"E5.sketch_text.stroke-77"),sQuery(id+"F12.wireOp",EDGE,"E5.sketch_text.stroke-78"),sQuery(id+"F12.wireOp",EDGE,"E5.sketch_text.stroke-79"),sQuery(id+"F12.wireOp",EDGE,"E5.sketch_text.stroke-80"),sQuery(id+"F12.wireOp",EDGE,"E5.sketch_text.stroke-81")])]});
            var Q5;
            Q5=makeQuery(id+"F13.opExtrude","SWEPT_BODY",BODY,{"disambiguationData":[OSD([sQuery(id+"F12.wireOp",EDGE,"E5.sketch_text.stroke-82"),sQuery(id+"F12.wireOp",EDGE,"E5.sketch_text.stroke-83"),sQuery(id+"F12.wireOp",EDGE,"E5.sketch_text.stroke-84"),sQuery(id+"F12.wireOp",EDGE,"E5.sketch_text.stroke-85"),sQuery(id+"F12.wireOp",EDGE,"E5.sketch_text.stroke-86"),sQuery(id+"F12.wireOp",EDGE,"E5.sketch_text.stroke-87"),sQuery(id+"F12.wireOp",EDGE,"E5.sketch_text.stroke-88"),sQuery(id+"F12.wireOp",EDGE,"E5.sketch_text.stroke-89"),sQuery(id+"F12.wireOp",EDGE,"E5.sketch_text.stroke-90")])]});
            var Q6;
            Q6=makeQuery(id+"F13.opExtrude","SWEPT_BODY",BODY,{"disambiguationData":[OSD([sQuery(id+"F12.wireOp",EDGE,"E5.sketch_text.stroke-91"),sQuery(id+"F12.wireOp",EDGE,"E5.sketch_text.stroke-92"),sQuery(id+"F12.wireOp",EDGE,"E5.sketch_text.stroke-93"),sQuery(id+"F12.wireOp",EDGE,"E5.sketch_text.stroke-94"),sQuery(id+"F12.wireOp",EDGE,"E5.sketch_text.stroke-95"),sQuery(id+"F12.wireOp",EDGE,"E5.sketch_text.stroke-96"),sQuery(id+"F12.wireOp",EDGE,"E5.sketch_text.stroke-97"),sQuery(id+"F12.wireOp",EDGE,"E5.sketch_text.stroke-98"),sQuery(id+"F12.wireOp",EDGE,"E5.sketch_text.stroke-99"),sQuery(id+"F12.wireOp",EDGE,"E5.sketch_text.stroke-100"),sQuery(id+"F12.wireOp",EDGE,"E5.sketch_text.stroke-101"),sQuery(id+"F12.wireOp",EDGE,"E5.sketch_text.stroke-102"),sQuery(id+"F12.wireOp",EDGE,"E5.sketch_text.stroke-103"),sQuery(id+"F12.wireOp",EDGE,"E5.sketch_text.stroke-104"),sQuery(id+"F12.wireOp",EDGE,"E5.sketch_text.stroke-105"),sQuery(id+"F12.wireOp",EDGE,"E5.sketch_text.stroke-106"),sQuery(id+"F12.wireOp",EDGE,"E5.sketch_text.stroke-107"),sQuery(id+"F12.wireOp",EDGE,"E5.sketch_text.stroke-108")])]});
            var Q7;
            Q7=makeQuery(id+"F13.opExtrude","SWEPT_BODY",BODY,{"disambiguationData":[OSD([sQuery(id+"F12.wireOp",EDGE,"E5.sketch_text.stroke-109"),sQuery(id+"F12.wireOp",EDGE,"E5.sketch_text.stroke-110"),sQuery(id+"F12.wireOp",EDGE,"E5.sketch_text.stroke-111"),sQuery(id+"F12.wireOp",EDGE,"E5.sketch_text.stroke-112"),sQuery(id+"F12.wireOp",EDGE,"E5.sketch_text.stroke-113"),sQuery(id+"F12.wireOp",EDGE,"E5.sketch_text.stroke-114"),sQuery(id+"F12.wireOp",EDGE,"E5.sketch_text.stroke-115"),sQuery(id+"F12.wireOp",EDGE,"E5.sketch_text.stroke-116"),sQuery(id+"F12.wireOp",EDGE,"E5.sketch_text.stroke-117"),sQuery(id+"F12.wireOp",EDGE,"E5.sketch_text.stroke-118"),sQuery(id+"F12.wireOp",EDGE,"E5.sketch_text.stroke-119"),sQuery(id+"F12.wireOp",EDGE,"E5.sketch_text.stroke-120"),sQuery(id+"F12.wireOp",EDGE,"E5.sketch_text.stroke-121"),sQuery(id+"F12.wireOp",EDGE,"E5.sketch_text.stroke-122"),sQuery(id+"F12.wireOp",EDGE,"E5.sketch_text.stroke-123"),sQuery(id+"F12.wireOp",EDGE,"E5.sketch_text.stroke-124"),sQuery(id+"F12.wireOp",EDGE,"E5.sketch_text.stroke-125")])]});
            var Q8;
            Q8=makeQuery(id+"F13.opExtrude","SWEPT_BODY",BODY,{"disambiguationData":[OSD([sQuery(id+"F12.wireOp",EDGE,"E5.sketch_text.stroke-126"),sQuery(id+"F12.wireOp",EDGE,"E5.sketch_text.stroke-127"),sQuery(id+"F12.wireOp",EDGE,"E5.sketch_text.stroke-128"),sQuery(id+"F12.wireOp",EDGE,"E5.sketch_text.stroke-129"),sQuery(id+"F12.wireOp",EDGE,"E5.sketch_text.stroke-130"),sQuery(id+"F12.wireOp",EDGE,"E5.sketch_text.stroke-131"),sQuery(id+"F12.wireOp",EDGE,"E5.sketch_text.stroke-132"),sQuery(id+"F12.wireOp",EDGE,"E5.sketch_text.stroke-133"),sQuery(id+"F12.wireOp",EDGE,"E5.sketch_text.stroke-134"),sQuery(id+"F12.wireOp",EDGE,"E5.sketch_text.stroke-135"),sQuery(id+"F12.wireOp",EDGE,"E5.sketch_text.stroke-136"),sQuery(id+"F12.wireOp",EDGE,"E5.sketch_text.stroke-137"),sQuery(id+"F12.wireOp",EDGE,"E5.sketch_text.stroke-138"),sQuery(id+"F12.wireOp",EDGE,"E5.sketch_text.stroke-139")])]});
            var Q9;
            Q9=makeQuery(id+"F13.opExtrude","SWEPT_BODY",BODY,{"disambiguationData":[OSD([sQuery(id+"F12.wireOp",EDGE,"E5.sketch_text.stroke-140"),sQuery(id+"F12.wireOp",EDGE,"E5.sketch_text.stroke-141"),sQuery(id+"F12.wireOp",EDGE,"E5.sketch_text.stroke-142"),sQuery(id+"F12.wireOp",EDGE,"E5.sketch_text.stroke-143"),sQuery(id+"F12.wireOp",EDGE,"E5.sketch_text.stroke-144"),sQuery(id+"F12.wireOp",EDGE,"E5.sketch_text.stroke-145"),sQuery(id+"F12.wireOp",EDGE,"E5.sketch_text.stroke-146"),sQuery(id+"F12.wireOp",EDGE,"E5.sketch_text.stroke-147"),sQuery(id+"F12.wireOp",EDGE,"E5.sketch_text.stroke-148"),sQuery(id+"F12.wireOp",EDGE,"E5.sketch_text.stroke-149"),sQuery(id+"F12.wireOp",EDGE,"E5.sketch_text.stroke-150"),sQuery(id+"F12.wireOp",EDGE,"E5.sketch_text.stroke-151"),sQuery(id+"F12.wireOp",EDGE,"E5.sketch_text.stroke-152")])]});
            var Q10;
            Q10=makeQuery(id+"F13.opExtrude","SWEPT_BODY",BODY,{"disambiguationData":[OSD([sQuery(id+"F12.wireOp",EDGE,"E5.sketch_text.stroke-153"),sQuery(id+"F12.wireOp",EDGE,"E5.sketch_text.stroke-154"),sQuery(id+"F12.wireOp",EDGE,"E5.sketch_text.stroke-155"),sQuery(id+"F12.wireOp",EDGE,"E5.sketch_text.stroke-156"),sQuery(id+"F12.wireOp",EDGE,"E5.sketch_text.stroke-157"),sQuery(id+"F12.wireOp",EDGE,"E5.sketch_text.stroke-158"),sQuery(id+"F12.wireOp",EDGE,"E5.sketch_text.stroke-159"),sQuery(id+"F12.wireOp",EDGE,"E5.sketch_text.stroke-160"),sQuery(id+"F12.wireOp",EDGE,"E5.sketch_text.stroke-161"),sQuery(id+"F12.wireOp",EDGE,"E5.sketch_text.stroke-162"),sQuery(id+"F12.wireOp",EDGE,"E5.sketch_text.stroke-163"),sQuery(id+"F12.wireOp",EDGE,"E5.sketch_text.stroke-164"),sQuery(id+"F12.wireOp",EDGE,"E5.sketch_text.stroke-165"),sQuery(id+"F12.wireOp",EDGE,"E5.sketch_text.stroke-166"),sQuery(id+"F12.wireOp",EDGE,"E5.sketch_text.stroke-167"),sQuery(id+"F12.wireOp",EDGE,"E5.sketch_text.stroke-168"),sQuery(id+"F12.wireOp",EDGE,"E5.sketch_text.stroke-169"),sQuery(id+"F12.wireOp",EDGE,"E5.sketch_text.stroke-170"),sQuery(id+"F12.wireOp",EDGE,"E5.sketch_text.stroke-171"),sQuery(id+"F12.wireOp",EDGE,"E5.sketch_text.stroke-172")])]});
            var Q11;
            Q11=makeQuery(id+"F13.opExtrude","SWEPT_BODY",BODY,{"disambiguationData":[OSD([sQuery(id+"F12.wireOp",EDGE,"E5.sketch_text.stroke-173"),sQuery(id+"F12.wireOp",EDGE,"E5.sketch_text.stroke-174"),sQuery(id+"F12.wireOp",EDGE,"E5.sketch_text.stroke-175"),sQuery(id+"F12.wireOp",EDGE,"E5.sketch_text.stroke-176"),sQuery(id+"F12.wireOp",EDGE,"E5.sketch_text.stroke-177"),sQuery(id+"F12.wireOp",EDGE,"E5.sketch_text.stroke-178"),sQuery(id+"F12.wireOp",EDGE,"E5.sketch_text.stroke-179"),sQuery(id+"F12.wireOp",EDGE,"E5.sketch_text.stroke-180"),sQuery(id+"F12.wireOp",EDGE,"E5.sketch_text.stroke-181"),sQuery(id+"F12.wireOp",EDGE,"E5.sketch_text.stroke-182"),sQuery(id+"F12.wireOp",EDGE,"E5.sketch_text.stroke-183"),sQuery(id+"F12.wireOp",EDGE,"E5.sketch_text.stroke-184"),sQuery(id+"F12.wireOp",EDGE,"E5.sketch_text.stroke-185"),sQuery(id+"F12.wireOp",EDGE,"E5.sketch_text.stroke-186"),sQuery(id+"F12.wireOp",EDGE,"E5.sketch_text.stroke-187"),sQuery(id+"F12.wireOp",EDGE,"E5.sketch_text.stroke-188"),sQuery(id+"F12.wireOp",EDGE,"E5.sketch_text.stroke-189"),sQuery(id+"F12.wireOp",EDGE,"E5.sketch_text.stroke-190"),sQuery(id+"F12.wireOp",EDGE,"E5.sketch_text.stroke-191"),sQuery(id+"F12.wireOp",EDGE,"E5.sketch_text.stroke-192"),sQuery(id+"F12.wireOp",EDGE,"E5.sketch_text.stroke-193"),sQuery(id+"F12.wireOp",EDGE,"E5.sketch_text.stroke-194"),sQuery(id+"F12.wireOp",EDGE,"E5.sketch_text.stroke-195"),sQuery(id+"F12.wireOp",EDGE,"E5.sketch_text.stroke-196"),sQuery(id+"F12.wireOp",EDGE,"E5.sketch_text.stroke-197"),sQuery(id+"F12.wireOp",EDGE,"E5.sketch_text.stroke-198"),sQuery(id+"F12.wireOp",EDGE,"E5.sketch_text.stroke-199"),sQuery(id+"F12.wireOp",EDGE,"E5.sketch_text.stroke-200")])]});
            var Q12;
            Q12=makeQuery(id+"F13.opExtrude","SWEPT_BODY",BODY,{"disambiguationData":[OSD([sQuery(id+"F12.wireOp",EDGE,"E5.sketch_text.stroke-201"),sQuery(id+"F12.wireOp",EDGE,"E5.sketch_text.stroke-202"),sQuery(id+"F12.wireOp",EDGE,"E5.sketch_text.stroke-203"),sQuery(id+"F12.wireOp",EDGE,"E5.sketch_text.stroke-204"),sQuery(id+"F12.wireOp",EDGE,"E5.sketch_text.stroke-205"),sQuery(id+"F12.wireOp",EDGE,"E5.sketch_text.stroke-206")])]});
            var Q13;
            Q13=makeQuery(id+"F13.opExtrude","SWEPT_BODY",BODY,{"disambiguationData":[OSD([sQuery(id+"F12.wireOp",EDGE,"E5.sketch_text.stroke-207"),sQuery(id+"F12.wireOp",EDGE,"E5.sketch_text.stroke-208"),sQuery(id+"F12.wireOp",EDGE,"E5.sketch_text.stroke-209"),sQuery(id+"F12.wireOp",EDGE,"E5.sketch_text.stroke-210"),sQuery(id+"F12.wireOp",EDGE,"E5.sketch_text.stroke-211")])]});
            var Q14;
            Q14=makeQuery(id+"F13.opExtrude","SWEPT_BODY",BODY,{"disambiguationData":[OSD([sQuery(id+"F12.wireOp",EDGE,"E5.sketch_text.stroke-212"),sQuery(id+"F12.wireOp",EDGE,"E5.sketch_text.stroke-213"),sQuery(id+"F12.wireOp",EDGE,"E5.sketch_text.stroke-214"),sQuery(id+"F12.wireOp",EDGE,"E5.sketch_text.stroke-215")])]});
            var Q15;
            Q15=makeQuery(id+"F13.opExtrude","SWEPT_BODY",BODY,{"disambiguationData":[OSD([sQuery(id+"F12.wireOp",EDGE,"E5.sketch_text.stroke-216"),sQuery(id+"F12.wireOp",EDGE,"E5.sketch_text.stroke-217"),sQuery(id+"F12.wireOp",EDGE,"E5.sketch_text.stroke-218"),sQuery(id+"F12.wireOp",EDGE,"E5.sketch_text.stroke-219"),sQuery(id+"F12.wireOp",EDGE,"E5.sketch_text.stroke-220"),sQuery(id+"F12.wireOp",EDGE,"E5.sketch_text.stroke-221"),sQuery(id+"F12.wireOp",EDGE,"E5.sketch_text.stroke-222"),sQuery(id+"F12.wireOp",EDGE,"E5.sketch_text.stroke-223"),sQuery(id+"F12.wireOp",EDGE,"E5.sketch_text.stroke-224"),sQuery(id+"F12.wireOp",EDGE,"E5.sketch_text.stroke-225"),sQuery(id+"F12.wireOp",EDGE,"E5.sketch_text.stroke-226"),sQuery(id+"F12.wireOp",EDGE,"E5.sketch_text.stroke-227"),sQuery(id+"F12.wireOp",EDGE,"E5.sketch_text.stroke-228"),sQuery(id+"F12.wireOp",EDGE,"E5.sketch_text.stroke-229"),sQuery(id+"F12.wireOp",EDGE,"E5.sketch_text.stroke-230"),sQuery(id+"F12.wireOp",EDGE,"E5.sketch_text.stroke-231"),sQuery(id+"F12.wireOp",EDGE,"E5.sketch_text.stroke-232"),sQuery(id+"F12.wireOp",EDGE,"E5.sketch_text.stroke-233"),sQuery(id+"F12.wireOp",EDGE,"E5.sketch_text.stroke-234"),sQuery(id+"F12.wireOp",EDGE,"E5.sketch_text.stroke-235"),sQuery(id+"F12.wireOp",EDGE,"E5.sketch_text.stroke-236"),sQuery(id+"F12.wireOp",EDGE,"E5.sketch_text.stroke-237"),sQuery(id+"F12.wireOp",EDGE,"E5.sketch_text.stroke-238")])]});
            var Q16;
            Q16=makeQuery(id+"F13.opExtrude","SWEPT_BODY",BODY,{"disambiguationData":[OSD([sQuery(id+"F12.wireOp",EDGE,"E5.sketch_text.stroke-239"),sQuery(id+"F12.wireOp",EDGE,"E5.sketch_text.stroke-240"),sQuery(id+"F12.wireOp",EDGE,"E5.sketch_text.stroke-241"),sQuery(id+"F12.wireOp",EDGE,"E5.sketch_text.stroke-242"),sQuery(id+"F12.wireOp",EDGE,"E5.sketch_text.stroke-243"),sQuery(id+"F12.wireOp",EDGE,"E5.sketch_text.stroke-244"),sQuery(id+"F12.wireOp",EDGE,"E5.sketch_text.stroke-245"),sQuery(id+"F12.wireOp",EDGE,"E5.sketch_text.stroke-246"),sQuery(id+"F12.wireOp",EDGE,"E5.sketch_text.stroke-247"),sQuery(id+"F12.wireOp",EDGE,"E5.sketch_text.stroke-248"),sQuery(id+"F12.wireOp",EDGE,"E5.sketch_text.stroke-249"),sQuery(id+"F12.wireOp",EDGE,"E5.sketch_text.stroke-250"),sQuery(id+"F12.wireOp",EDGE,"E5.sketch_text.stroke-251")])]});
            var Q17;
            Q17=makeQuery(id+"F13.opExtrude","SWEPT_BODY",BODY,{"disambiguationData":[OSD([sQuery(id+"F12.wireOp",EDGE,"E5.sketch_text.stroke-252"),sQuery(id+"F12.wireOp",EDGE,"E5.sketch_text.stroke-253"),sQuery(id+"F12.wireOp",EDGE,"E5.sketch_text.stroke-254"),sQuery(id+"F12.wireOp",EDGE,"E5.sketch_text.stroke-255"),sQuery(id+"F12.wireOp",EDGE,"E5.sketch_text.stroke-256"),sQuery(id+"F12.wireOp",EDGE,"E5.sketch_text.stroke-257"),sQuery(id+"F12.wireOp",EDGE,"E5.sketch_text.stroke-258"),sQuery(id+"F12.wireOp",EDGE,"E5.sketch_text.stroke-259"),sQuery(id+"F12.wireOp",EDGE,"E5.sketch_text.stroke-260"),sQuery(id+"F12.wireOp",EDGE,"E5.sketch_text.stroke-261"),sQuery(id+"F12.wireOp",EDGE,"E5.sketch_text.stroke-262"),sQuery(id+"F12.wireOp",EDGE,"E5.sketch_text.stroke-263"),sQuery(id+"F12.wireOp",EDGE,"E5.sketch_text.stroke-264"),sQuery(id+"F12.wireOp",EDGE,"E5.sketch_text.stroke-265"),sQuery(id+"F12.wireOp",EDGE,"E5.sketch_text.stroke-266"),sQuery(id+"F12.wireOp",EDGE,"E5.sketch_text.stroke-267"),sQuery(id+"F12.wireOp",EDGE,"E5.sketch_text.stroke-268"),sQuery(id+"F12.wireOp",EDGE,"E5.sketch_text.stroke-269"),sQuery(id+"F12.wireOp",EDGE,"E5.sketch_text.stroke-270"),sQuery(id+"F12.wireOp",EDGE,"E5.sketch_text.stroke-271"),sQuery(id+"F12.wireOp",EDGE,"E5.sketch_text.stroke-272"),sQuery(id+"F12.wireOp",EDGE,"E5.sketch_text.stroke-273"),sQuery(id+"F12.wireOp",EDGE,"E5.sketch_text.stroke-274"),sQuery(id+"F12.wireOp",EDGE,"E5.sketch_text.stroke-275"),sQuery(id+"F12.wireOp",EDGE,"E5.sketch_text.stroke-276")])]});
            var Q18;
            Q18=makeQuery(id+"F13.opExtrude","SWEPT_BODY",BODY,{"disambiguationData":[OSD([sQuery(id+"F12.wireOp",EDGE,"E5.sketch_text.stroke-277"),sQuery(id+"F12.wireOp",EDGE,"E5.sketch_text.stroke-278"),sQuery(id+"F12.wireOp",EDGE,"E5.sketch_text.stroke-279"),sQuery(id+"F12.wireOp",EDGE,"E5.sketch_text.stroke-280"),sQuery(id+"F12.wireOp",EDGE,"E5.sketch_text.stroke-281"),sQuery(id+"F12.wireOp",EDGE,"E5.sketch_text.stroke-282"),sQuery(id+"F12.wireOp",EDGE,"E5.sketch_text.stroke-283"),sQuery(id+"F12.wireOp",EDGE,"E5.sketch_text.stroke-284"),sQuery(id+"F12.wireOp",EDGE,"E5.sketch_text.stroke-285"),sQuery(id+"F12.wireOp",EDGE,"E5.sketch_text.stroke-286"),sQuery(id+"F12.wireOp",EDGE,"E5.sketch_text.stroke-287"),sQuery(id+"F12.wireOp",EDGE,"E5.sketch_text.stroke-288"),sQuery(id+"F12.wireOp",EDGE,"E5.sketch_text.stroke-289")])]});
            var Q19;
            Q19=makeQuery(id+"F13.opExtrude","SWEPT_BODY",BODY,{"disambiguationData":[OSD([sQuery(id+"F12.wireOp",EDGE,"E5.sketch_text.stroke-290"),sQuery(id+"F12.wireOp",EDGE,"E5.sketch_text.stroke-291"),sQuery(id+"F12.wireOp",EDGE,"E5.sketch_text.stroke-292"),sQuery(id+"F12.wireOp",EDGE,"E5.sketch_text.stroke-293"),sQuery(id+"F12.wireOp",EDGE,"E5.sketch_text.stroke-294"),sQuery(id+"F12.wireOp",EDGE,"E5.sketch_text.stroke-295"),sQuery(id+"F12.wireOp",EDGE,"E5.sketch_text.stroke-296"),sQuery(id+"F12.wireOp",EDGE,"E5.sketch_text.stroke-297"),sQuery(id+"F12.wireOp",EDGE,"E5.sketch_text.stroke-298"),sQuery(id+"F12.wireOp",EDGE,"E5.sketch_text.stroke-299"),sQuery(id+"F12.wireOp",EDGE,"E5.sketch_text.stroke-300"),sQuery(id+"F12.wireOp",EDGE,"E5.sketch_text.stroke-301"),sQuery(id+"F12.wireOp",EDGE,"E5.sketch_text.stroke-302"),sQuery(id+"F12.wireOp",EDGE,"E5.sketch_text.stroke-303"),sQuery(id+"F12.wireOp",EDGE,"E5.sketch_text.stroke-304"),sQuery(id+"F12.wireOp",EDGE,"E5.sketch_text.stroke-305"),sQuery(id+"F12.wireOp",EDGE,"E5.sketch_text.stroke-306")])]});
            var Q20;
            Q20=makeQuery(id+"F13.opExtrude","SWEPT_BODY",BODY,{"disambiguationData":[OSD([sQuery(id+"F12.wireOp",EDGE,"E5.sketch_text.stroke-307"),sQuery(id+"F12.wireOp",EDGE,"E5.sketch_text.stroke-308"),sQuery(id+"F12.wireOp",EDGE,"E5.sketch_text.stroke-309"),sQuery(id+"F12.wireOp",EDGE,"E5.sketch_text.stroke-310")])]});
            var Q21;
            Q21=makeQuery(id+"F13.opExtrude","SWEPT_BODY",BODY,{"disambiguationData":[OSD([sQuery(id+"F12.wireOp",EDGE,"E5.sketch_text.stroke-311"),sQuery(id+"F12.wireOp",EDGE,"E5.sketch_text.stroke-312"),sQuery(id+"F12.wireOp",EDGE,"E5.sketch_text.stroke-313"),sQuery(id+"F12.wireOp",EDGE,"E5.sketch_text.stroke-314"),sQuery(id+"F12.wireOp",EDGE,"E5.sketch_text.stroke-315"),sQuery(id+"F12.wireOp",EDGE,"E5.sketch_text.stroke-316"),sQuery(id+"F12.wireOp",EDGE,"E5.sketch_text.stroke-317"),sQuery(id+"F12.wireOp",EDGE,"E5.sketch_text.stroke-318")])]});
            transform(context, id + "F15", {"entities" : qUnion([Q0, Q1, Q2, Q3, Q4, Q5, Q6, Q7, Q8, Q9, Q10, Q11, Q12, Q13, Q14, Q15, Q16, Q17, Q18, Q19, Q20, Q21]), "transformType" : TransformType.TRANSLATION_3D, "dx" : -127.25 * mm, "dy" : 23.37 * mm, "dz" : 0 * mm, "makeCopy" : false});
        }
    });
